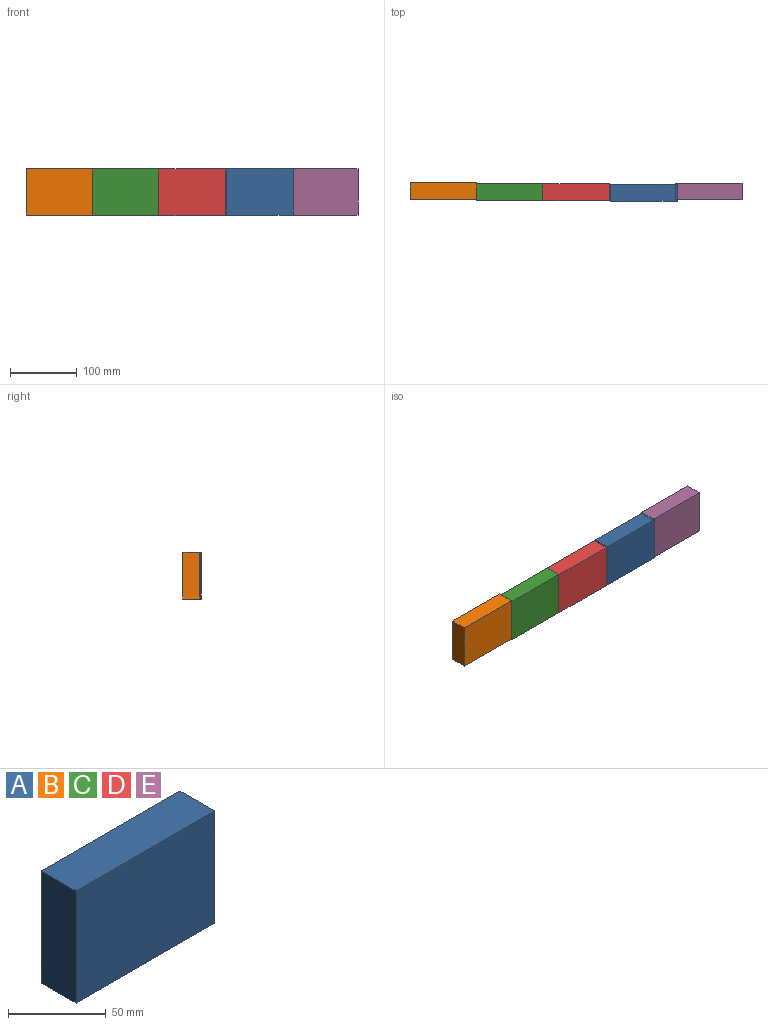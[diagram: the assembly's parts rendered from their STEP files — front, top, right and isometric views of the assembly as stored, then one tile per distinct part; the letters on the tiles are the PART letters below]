
ASSEMBLY  parts=5 mates=1
PART A: 6 faces, bbox 100x25x70 mm
  f0: plane 70x25mm, normal (1,0,0), area 1750mm2, adj f1,f3,f4,f5
  f1: plane 100x25mm, normal (0,0,1), area 2500mm2, adj f0,f2,f4,f5
  f2: plane 70x25mm, normal (-1,0,0), area 1750mm2, adj f1,f3,f4,f5
  f3: plane 100x25mm, normal (0,0,-1), area 2500mm2, adj f0,f2,f4,f5
  f4: plane 100x70mm, normal (0,-1,0), area 7000mm2, adj f0,f1,f2,f3
  f5: plane 100x70mm, normal (0,1,0), area 7000mm2, adj f0,f1,f2,f3
PART B: same geometry as A
PART C: same geometry as A
PART D: same geometry as A
PART E: same geometry as A
PLACE A t=(-10,20.41,-170.7)mm fixed
PLACE B t=(-310.61,22.76,-170.63)mm fixed
PLACE C t=(-211.42,21.35,-171.6)mm
PLACE D t=(-111.42,21.35,-171.6)mm fixed
PLACE E t=(87.25,22.19,-170.91)mm fixed
MATE fastened C.f0 <-> D.f2  axis (1,0,0) through (-161.42,8.85,-171.6)mm
